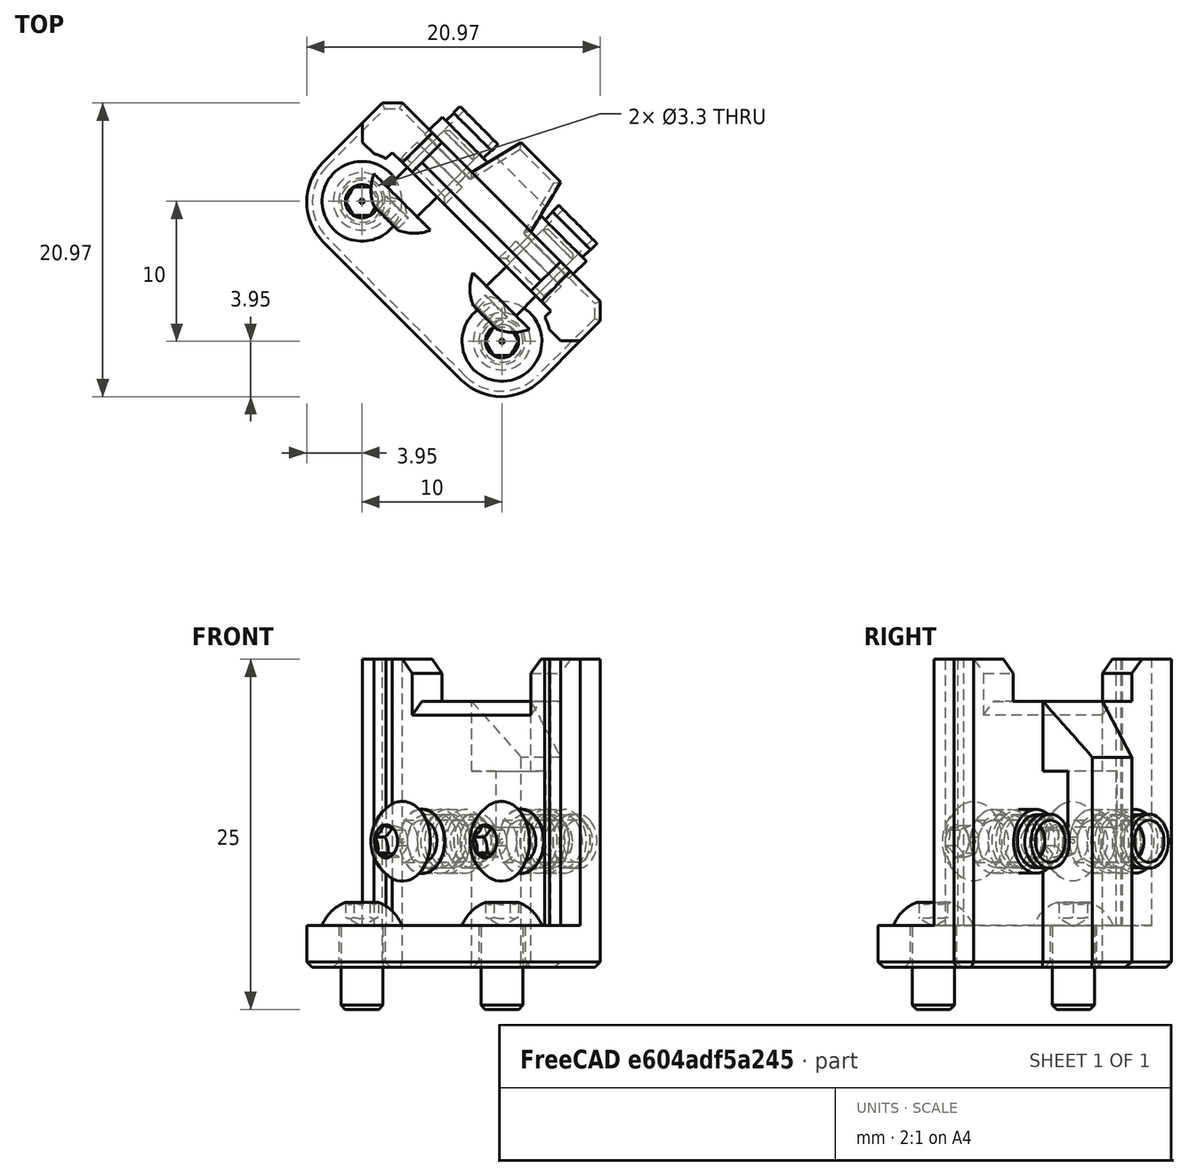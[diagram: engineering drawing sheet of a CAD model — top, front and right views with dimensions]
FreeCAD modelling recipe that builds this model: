
FCSTD DOCUMENT  (FreeCAD 0.19R24291 (Git))
Label: addon-chamber-temp-sensor-assembly
License: All rights reserved
LicenseURL: http://en.wikipedia.org/wiki/All_rights_reserved
objects: Part::FeaturePython×6, PartDesign::CoordinateSystem×1, Part::Feature×1, App::Part×1
note: 8 computed .brp shape members not serialized (recipe doc carries the construction recipe); baked Part::Feature solids carry a one-line shape summary decoded from their .brp

FEATURE [Part::FeaturePython] HeatSet  label="M3x3-HeatSet"  # WARN: FeaturePython — macro-defined, semantics opaque (R4)
  Placement = pos=(-0.707107,6.36396,9) rot=(0.707107,-0.707107,0;1.5708rad)
  baseObject = -> Body001001 [Edge43]
  diameter = 2
  invert = false
  offset = 0
FEATURE [Part::FeaturePython] Screw  label="M3x6-Screw"  # Fasteners workbench fastener (typed FeaturePython)
  Placement = pos=(-4.99995,4.99995,3) rot=(0,0,1;0rad)
  baseObject = -> Body001001 [Edge138]
  diameter = 1
  invert = true
  length = 0
  lengthCustom = 6
  matchOuter = true
  offset = 0
  thread = false
  type = 40
FEATURE [Part::FeaturePython] HeatSet001  label="M3x3-HeatSet001"  # WARN: FeaturePython — macro-defined, semantics opaque (R4)
  Placement = pos=(6.36396,-0.707107,9) rot=(0.707107,-0.707107,0;1.5708rad)
  baseObject = -> Body001001 [Edge44]
  diameter = 2
  invert = false
  offset = 0
FEATURE [Part::FeaturePython] Screw002  label="M3x6-Screw007"  # Fasteners workbench fastener (typed FeaturePython)
  Placement = pos=(-2.12132,4.94975,9) rot=(0.707107,-0.707107,0;1.5708rad)
  baseObject = -> HeatSet [Edge1]
  diameter = 1
  invert = false
  length = 0
  lengthCustom = 6
  matchOuter = true
  offset = 2
  thread = false
  type = 40
FEATURE [Part::FeaturePython] Screw003  label="M3x6-Screw008"  # Fasteners workbench fastener (typed FeaturePython)
  Placement = pos=(4.94975,-2.12132,9) rot=(0.707107,-0.707107,0;1.5708rad)
  baseObject = -> HeatSet001 [Edge1]
  diameter = 1
  invert = false
  length = 0
  lengthCustom = 6
  matchOuter = true
  offset = 2
  thread = false
  type = 40
FEATURE [PartDesign::CoordinateSystem] LCS_chamber_temp_sensor  label="LCS_chamber-temp-sensor"
  AttacherType = Attacher::AttachEngine3D
FEATURE [Part::FeaturePython] Screw001  label="M3x6-Screw006"  # Fasteners workbench fastener (typed FeaturePython)
  Placement = pos=(4.99995,-4.99995,3) rot=(0,0,1;0rad)
  baseObject = -> Body001001 [Edge134]
  diameter = 1
  invert = true
  length = 0
  lengthCustom = 6
  matchOuter = true
  offset = 0
  thread = false
  type = 40
FEATURE [Part::Feature] Body001001  label="HTU21D-mounter"
  Placement = pos=(0,0,0) rot=(0,0,-1;0.785398rad)
  shape: bbox 20.97 x 20.97 x 22 mm, 55 faces (baked)
FEATURE [App::Part] Part  label="chamber-temp-sensor"
  Group = -> [Body001001,HeatSet001,HeatSet,Screw,Screw001,Screw002,Screw003,LCS_chamber_temp_sensor]
  Origin = -> Origin
